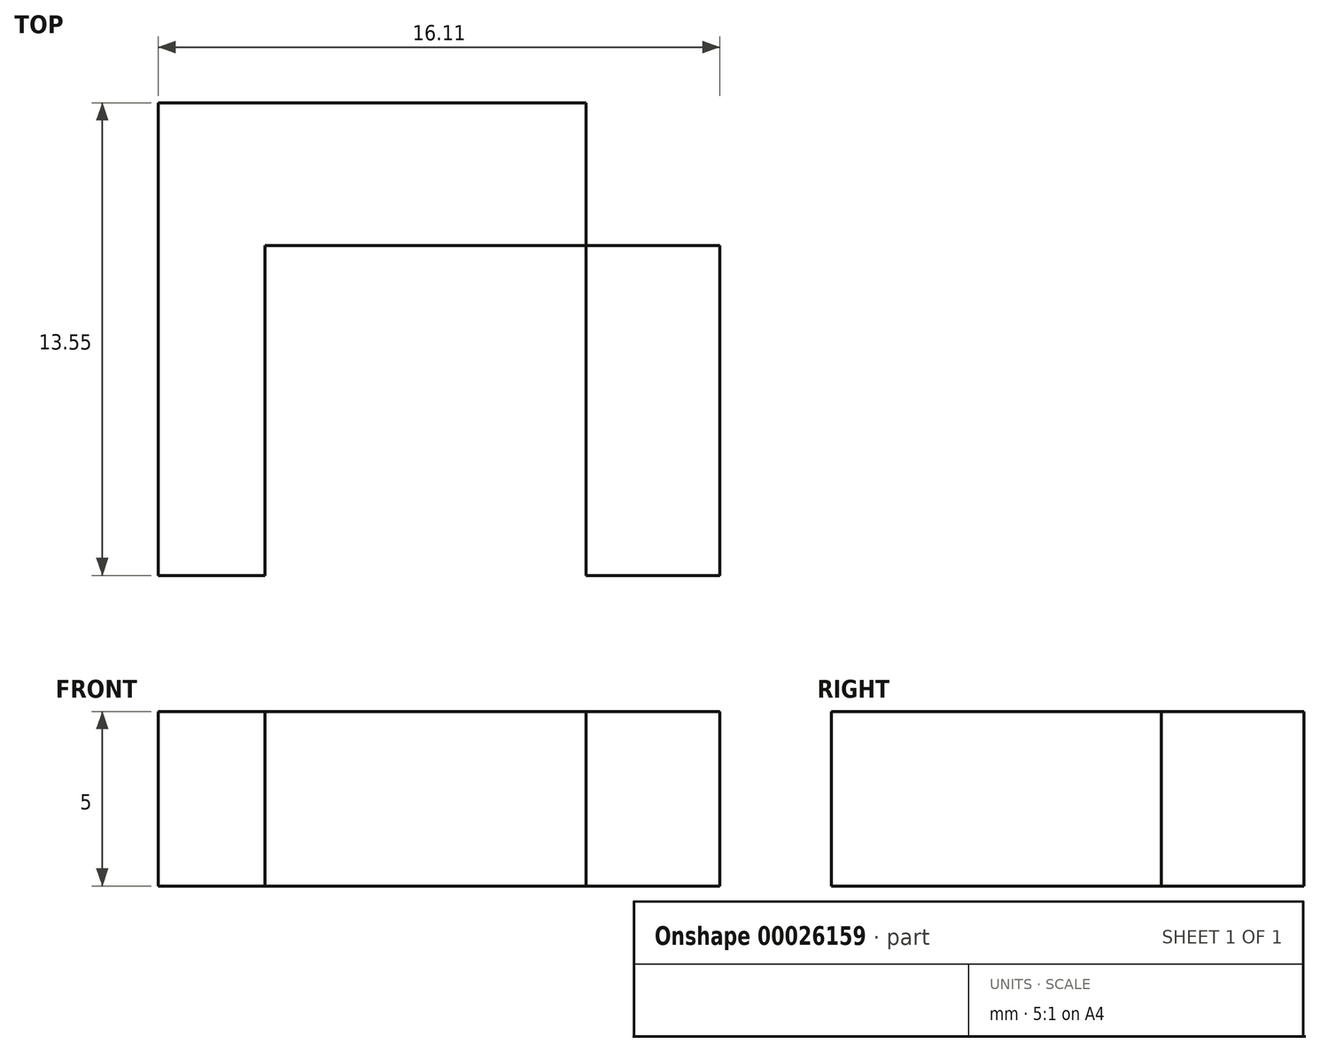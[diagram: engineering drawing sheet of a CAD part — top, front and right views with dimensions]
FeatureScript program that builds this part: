
annotation { "Feature Type Name" : "Feature", "Feature Type Description" : "" }
export const myFeature = defineFeature(function(context is Context, id is Id, definition is map)
    precondition{}
    {
        {
            var Q0;
            Q0=qCreatedBy(makeId("Top.planeOp"),FACE);
            var sketch = newSketch(context, id + "F0", { "sketchPlane" : qUnion([Q0])});
            skLineSegment(sketch, "E0.bottom", {"start": v(-13.04, 0) * mm, "end": v(-16.88, 0) * mm});
            skLineSegment(sketch, "E0.top", {"start": v(-13.04, 13.55) * mm, "end": v(-16.88, 13.55) * mm});
            skLineSegment(sketch, "E0.left", {"start": v(-13.04, 0) * mm, "end": v(-13.04, 13.55) * mm});
            skLineSegment(sketch, "E0.right", {"start": v(-16.88, 0) * mm, "end": v(-16.88, 13.55) * mm});
            skLineSegment(sketch, "E1.bottom", {"start": v(-16.88, 13.55) * mm, "end": v(-13.04, 13.55) * mm});
            skLineSegment(sketch, "E1.top", {"start": v(-16.88, 13.55) * mm, "end": v(-13.04, 13.55) * mm});
            skLineSegment(sketch, "E1.left", {"start": v(-16.88, 13.55) * mm, "end": v(-16.88, 13.55) * mm});
            skLineSegment(sketch, "E1.right", {"start": v(-13.04, 13.55) * mm, "end": v(-13.04, 13.55) * mm});
            skLineSegment(sketch, "E2.bottom", {"start": v(-13.04, 13.55) * mm, "end": v(-26.08, 13.55) * mm});
            skLineSegment(sketch, "E2.top", {"start": v(-13.04, 9.46) * mm, "end": v(-26.08, 9.46) * mm});
            skLineSegment(sketch, "E2.left", {"start": v(-13.04, 13.55) * mm, "end": v(-13.04, 9.46) * mm});
            skLineSegment(sketch, "E2.right", {"start": v(-26.08, 13.55) * mm, "end": v(-26.08, 9.46) * mm});
            skLineSegment(sketch, "E3.bottom", {"start": v(-26.08, 13.55) * mm, "end": v(-29.15, 13.55) * mm});
            skLineSegment(sketch, "E3.top", {"start": v(-26.08, 0) * mm, "end": v(-29.15, 0) * mm});
            skLineSegment(sketch, "E3.left", {"start": v(-26.08, 13.55) * mm, "end": v(-26.08, 0) * mm});
            skLineSegment(sketch, "E3.right", {"start": v(-29.15, 13.55) * mm, "end": v(-29.15, 0) * mm});
            skSolve(sketch);
        }
        {
            var Q0;
            {var subQ4=sQuery(id+"F0.wireOp",EDGE,"E0.bottom");Q0=makeQuery(id+"F0.imprint","IMPRINT",FACE,{"disambiguationData":[TD([[makeQuery(id+"F0.imprint","IMPRINT",EDGE,{"derivedFrom":subQ4}),-1.0]])]});}
            var Q1;
            {var subQ3=sQuery(id+"F0.wireOp",EDGE,"E3.bottom");Q1=makeQuery(id+"F0.imprint","IMPRINT",FACE,{"disambiguationData":[TD([[makeQuery(id+"F0.imprint","IMPRINT",EDGE,{"derivedFrom":subQ3}),1.0]])]});}
            var Q2;
            {var subQ0=sQuery(id+"F0.wireOp",EDGE,"E2.left");Q2=makeQuery(id+"F0.imprint","IMPRINT",FACE,{"disambiguationData":[TD([[makeQuery(id+"F0.imprint","IMPRINT",EDGE,{"derivedFrom":subQ0}),-1.0]])]});}
            var Q3;
            {var subQ3=sQuery(id+"F0.wireOp",EDGE,"E2.bottom");var subQ5=sQuery(id+"F0.wireOp",EDGE,"E0.right");var subQ7=makeQuery(id+"F0.imprint","INTERSECT",VERTEX,{"derivedFrom":[subQ5,subQ3]});Q3=makeQuery(id+"F0.imprint","IMPRINT",FACE,{"disambiguationData":[TD([[makeQuery(id+"F0.imprint","IMPRINT",EDGE,{"disambiguationData":[TD([[subQ7,1.0]])],"derivedFrom":subQ5}),1.0]])]});}
            extrude(context, id + "F1", {"entities" : qUnion([Q0, Q1, Q2, Q3]), "depth" : 5 * mm});
        }
    });
